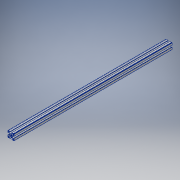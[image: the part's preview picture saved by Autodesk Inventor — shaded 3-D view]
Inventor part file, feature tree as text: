
AUTODESK INVENTOR PART (.ipt)
format: ipt  version: 2016 (Build 200138000, 138)  size: 1,083,904 bytes
history: native  units: in
note: dims shown in document units (in); Inventor stores cm internally (conversion verified against a paired STEP export)
features: extrude x1, sketch x1
ambient origin geometry x8: Origin, YZ Plane, XZ Plane, XY Plane, X Axis, Y Axis, Z Axis, Center Point
bodies: Solid1 (feature_tree)
feature tree (2):
  extrude  "Extrusion1"  [1 undecoded]
  sketch  "Sketch1"  dims[d0=29.5276in d1=0.0in]
note: 1 required parameter value undecoded (feature->parameter linkage not recoverable at this tier; creation-order binding heuristic only, values carry confidence <= 0.55)
